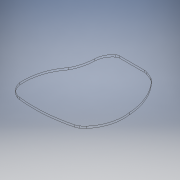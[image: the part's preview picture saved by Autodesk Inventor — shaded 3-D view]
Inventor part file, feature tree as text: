
AUTODESK INVENTOR PART (.ipt)
format: ipt  version: 2018 (Build 220112000, 112)  size: 174,592 bytes
history: native  units: in
note: dims shown in document units (in); Inventor stores cm internally (conversion verified against a paired STEP export)
features: fillet x6, extrude x2, sketch x2, imported_body x1
ambient origin geometry x8: Origin, YZ Plane, XZ Plane, XY Plane, X Axis, Y Axis, Z Axis, Center Point
bodies: Solid1 (feature_tree)
feature tree (11):
  imported_body  "Base1"
  extrude  "Extrusion1"  Depth=0.0197in
  fillet  "Fillet1"  Radius=0.0394in
  fillet  "Fillet2"  Radius=0.0394in
  fillet  "Fillet3"  Radius=0.0787in
  fillet  "Fillet4"  [1 undecoded]
  extrude  "Extrusion2"  Depth=0.0394in
  fillet  "Fillet6"  [1 undecoded]
  fillet  "Fillet7"  [1 undecoded]
  sketch  "Sketch1"  dims[d0=0.3937in d1=0.0in d2=0.0197in d3=0.0394in d4=0.0394in d5=0.0787in d6=0.0in d7=0.0in]
  sketch  "Sketch2"  dims[d9=0.0394in d10=0.0394in]
note: 3 required parameter values undecoded (feature->parameter linkage not recoverable at this tier; creation-order binding heuristic only, values carry confidence <= 0.55)
